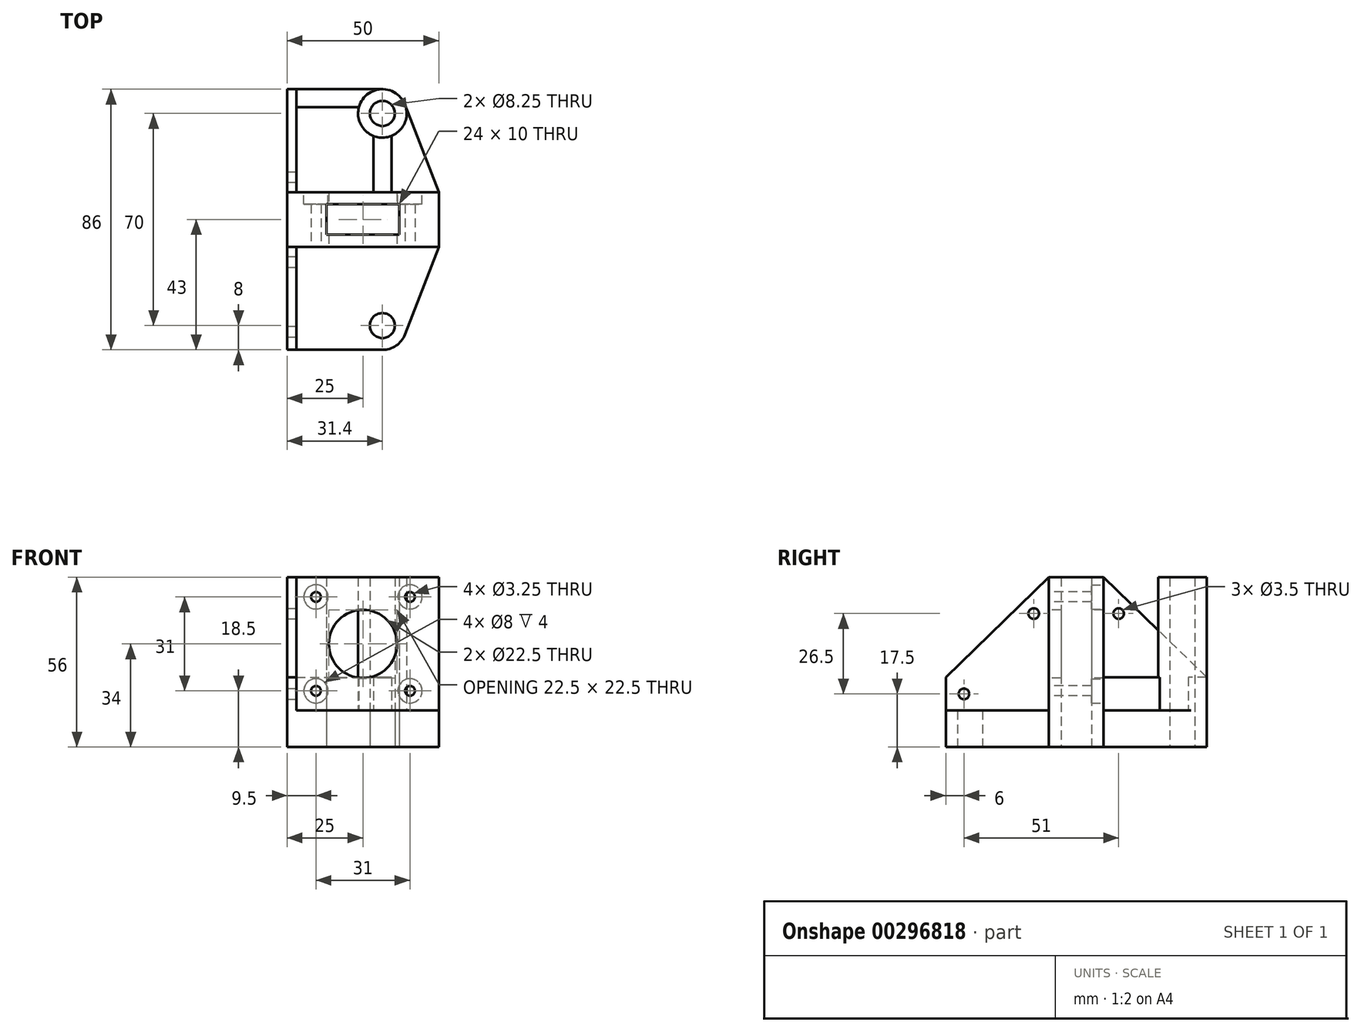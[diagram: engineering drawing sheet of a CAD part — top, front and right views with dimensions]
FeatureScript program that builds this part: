
annotation { "Feature Type Name" : "Feature", "Feature Type Description" : "" }
export const myFeature = defineFeature(function(context is Context, id is Id, definition is map)
    precondition{}
    {
        {
            var Q0;
            Q0=qCreatedBy(makeId("Top.planeOp"),FACE);
            var sketch = newSketch(context, id + "F0", { "sketchPlane" : qUnion([Q0])});
            skLineSegment(sketch, "E0.bottom", {"start": v(-25, 43) * mm, "end": v(6.4, 43) * mm});
            skLineSegment(sketch, "E0.top", {"start": v(-25, -43) * mm, "end": v(6.4, -43) * mm});
            skLineSegment(sketch, "E0.left", {"start": v(-25, 43) * mm, "end": v(-25, -43) * mm});
            skLineSegment(sketch, "E0.right", {"start": v(25, 9) * mm, "end": v(25, -9) * mm});
            skPoint(sketch, "E0.middle", {"position": v(0, 0) * mm});
            skArc(sketch, "E1", {"start": v(13.86, 37.88) * mm, "mid": v(10.93, 41.6) * mm, "end": v(6.4, 43) * mm});
            skLineSegment(sketch, "E2", {"start": v(0, 0) * mm, "end": v(-25, 0) * mm, "construction": true});
            skArc(sketch, "E3.MirrorC", {"start": v(13.86, -37.88) * mm, "mid": v(10.93, -41.6) * mm, "end": v(6.4, -43) * mm});
            skCircle(sketch, "E4", {"center": v(6.4, 35) * mm, "radius": 4.12 * mm});
            skCircle(sketch, "E5.MirrorC", {"center": v(6.4, -35) * mm, "radius": 4.12 * mm});
            skLineSegment(sketch, "E6.bottom", {"start": v(-12, 5) * mm, "end": v(12, 5) * mm});
            skLineSegment(sketch, "E6.top", {"start": v(-12, -5) * mm, "end": v(12, -5) * mm});
            skLineSegment(sketch, "E6.left", {"start": v(-12, 5) * mm, "end": v(-12, -5) * mm});
            skLineSegment(sketch, "E6.right", {"start": v(12, 5) * mm, "end": v(12, -5) * mm});
            skLineSegment(sketch, "E7", {"start": v(25, 9) * mm, "end": v(13.86, 37.88) * mm});
            skPoint(sketch, "E8.orphan", {"position": v(25, 43) * mm});
            skLineSegment(sketch, "E9.MirrorCS", {"start": v(25, -9) * mm, "end": v(13.86, -37.88) * mm});
            skPoint(sketch, "E10.orphan", {"position": v(25, -43) * mm});
            skSolve(sketch);
        }
        {
            var Q0;
            Q0=makeQuery(id+"F0.imprint","IMPRINT",FACE,{"disambiguationData":[TD([[makeQuery(id+"F0.imprint","IMPRINT",EDGE,{"derivedFrom":sQuery(id+"F0.wireOp",EDGE,"E0.bottom")}),-1.0]])]});
            extrude(context, id + "F1", {"entities" : qUnion([Q0]), "depth" : 12 * mm});
        }
        {
            var Q0;
            Q0=makeQuery(id+"F1.opExtrude","CAP_FACE",FACE,{"disambiguationData":[OSD([sQuery(id+"F0.wireOp",EDGE,"E0.bottom"),sQuery(id+"F0.wireOp",EDGE,"E0.top"),sQuery(id+"F0.wireOp",EDGE,"E0.left"),sQuery(id+"F0.wireOp",EDGE,"E0.right"),sQuery(id+"F0.wireOp",EDGE,"E1"),sQuery(id+"F0.wireOp",EDGE,"E3.MirrorC"),sQuery(id+"F0.wireOp",EDGE,"E4"),sQuery(id+"F0.wireOp",EDGE,"E5.MirrorC"),sQuery(id+"F0.wireOp",EDGE,"E6.bottom"),sQuery(id+"F0.wireOp",EDGE,"E6.top"),sQuery(id+"F0.wireOp",EDGE,"E6.left"),sQuery(id+"F0.wireOp",EDGE,"E6.right"),sQuery(id+"F0.wireOp",EDGE,"E7"),sQuery(id+"F0.wireOp",EDGE,"E9.MirrorCS")])],"isStart":false});
            var sketch = newSketch(context, id + "F2", { "sketchPlane" : qUnion([Q0])});
            skLineSegment(sketch, "E11.bottom", {"start": v(25, -9) * mm, "end": v(-25, -9) * mm});
            skLineSegment(sketch, "E11.top", {"start": v(25, 9) * mm, "end": v(-25, 9) * mm});
            skLineSegment(sketch, "E11.left", {"start": v(25, -9) * mm, "end": v(25, 9) * mm});
            skLineSegment(sketch, "E11.right", {"start": v(-25, -9) * mm, "end": v(-25, 9) * mm});
            skPoint(sketch, "E11.middle", {"position": v(0, 0) * mm});
            skLineSegment(sketch, "E12.0", {"start": v(-12, 5) * mm, "end": v(12, 5) * mm});
            skLineSegment(sketch, "E13.0", {"start": v(-12, 5) * mm, "end": v(-12, -5) * mm});
            skLineSegment(sketch, "E14.0", {"start": v(-12, -5) * mm, "end": v(12, -5) * mm});
            skLineSegment(sketch, "E15.0", {"start": v(12, 5) * mm, "end": v(12, -5) * mm});
            skSolve(sketch);
        }
        {
            var Q0;
            Q0=makeQuery(id+"F2.imprint","IMPRINT",FACE,{"disambiguationData":[TD([[makeQuery(id+"F2.imprint","IMPRINT",EDGE,{"derivedFrom":sQuery(id+"F2.wireOp",EDGE,"E11.bottom")}),-1.0]])]});
            extrude(context, id + "F3", {"entities" : qUnion([Q0]), "operationType" : NewBodyOperationType.ADD, "depth" : 44 * mm});
        }
        {
            var Q0;
            Q0=makeQuery(id+"F3.opExtrude","SWEPT_FACE",FACE,{"disambiguationData":[OSD([sQuery(id+"F2.wireOp",EDGE,"E11.bottom")])]});
            var sketch = newSketch(context, id + "F4", { "sketchPlane" : qUnion([Q0])});
            skLineSegment(sketch, "E16", {"start": v(-25, 34) * mm, "end": v(25, 34) * mm, "construction": true});
            skLineSegment(sketch, "E17", {"start": v(0, 56) * mm, "end": v(0, 12) * mm, "construction": true});
            skCircle(sketch, "E18", {"center": v(-15.5, 18.5) * mm, "radius": 1.63 * mm});
            skCircle(sketch, "E19.0.1.0", {"center": v(-15.5, 49.5) * mm, "radius": 1.63 * mm});
            skCircle(sketch, "E19.1.0.0", {"center": v(15.5, 18.5) * mm, "radius": 1.63 * mm});
            skCircle(sketch, "E19.1.1.0", {"center": v(15.5, 49.5) * mm, "radius": 1.63 * mm});
            skLineSegment(sketch, "E19.direction1", {"start": v(-15.5, 18.5) * mm, "end": v(15.5, 18.5) * mm, "construction": true});
            skLineSegment(sketch, "E19.direction2", {"start": v(-15.5, 18.5) * mm, "end": v(-15.5, 49.5) * mm, "construction": true});
            skCircle(sketch, "E20", {"center": v(0, 34) * mm, "radius": 11.25 * mm});
            skSolve(sketch);
        }
        {
            var Q0;
            Q0 = qSketchRegion(id + "F4", true);
            extrude(context, id + "F5", {"entities" : qUnion([Q0]), "operationType" : NewBodyOperationType.REMOVE, "endBound" : BoundingType.THROUGH_ALL, "oppositeDirection" : true, "depth" : 25 * mm});
        }
        {
            var Q0;
            Q0=makeQuery(id+"F3.boolean.opBoolean","MERGE",FACE,{"derivedFrom":[makeQuery(id+"F1.opExtrude","SWEPT_FACE",FACE,{"disambiguationData":[OSD([sQuery(id+"F0.wireOp",EDGE,"E0.left")])]}),makeQuery(id+"F3.opExtrude","SWEPT_FACE",FACE,{"disambiguationData":[OSD([sQuery(id+"F2.wireOp",EDGE,"E11.right")])]})]});
            var sketch = newSketch(context, id + "F6", { "sketchPlane" : qUnion([Q0])});
            skLineSegment(sketch, "E21.0", {"start": v(-43, 12) * mm, "end": v(-9, 12) * mm});
            skLineSegment(sketch, "E22.0", {"start": v(-9, 56) * mm, "end": v(-9, 12) * mm});
            skLineSegment(sketch, "E23.0", {"start": v(9, 56) * mm, "end": v(9, 12) * mm});
            skLineSegment(sketch, "E24.0", {"start": v(9, 12) * mm, "end": v(43, 12) * mm});
            skLineSegment(sketch, "E25", {"start": v(-43, 12) * mm, "end": v(-43, 23) * mm});
            skLineSegment(sketch, "E26", {"start": v(-43, 23) * mm, "end": v(-9, 56) * mm});
            skLineSegment(sketch, "E27", {"start": v(43, 12) * mm, "end": v(43, 23) * mm});
            skLineSegment(sketch, "E28", {"start": v(43, 23) * mm, "end": v(9, 56) * mm});
            skSolve(sketch);
        }
        {
            var Q0;
            Q0 = qSketchRegion(id + "F6", true);
            extrude(context, id + "F7", {"entities" : qUnion([Q0]), "operationType" : NewBodyOperationType.ADD, "oppositeDirection" : true, "depth" : 3 * mm});
        }
        {
            var Q0;
            {var subQ0=sQuery(id+"F0.wireOp",EDGE,"E1");var subQ1=sQuery(id+"F0.wireOp",EDGE,"E0.left");var subQ2=sQuery(id+"F0.wireOp",EDGE,"E0.right");var subQ3=sQuery(id+"F0.wireOp",EDGE,"E0.bottom");var subQ4=sQuery(id+"F0.wireOp",EDGE,"E4");var subQ5=sQuery(id+"F0.wireOp",EDGE,"E7");Q0=makeQuery(id+"F3.boolean.opBoolean","SPLIT",FACE,{"disambiguationData":[TD([makeQuery(id+"F1.opExtrude","SWEPT_FACE",FACE,{"disambiguationData":[OSD([subQ3])]})])],"derivedFrom":makeQuery(id+"F1.opExtrude","CAP_FACE",FACE,{"disambiguationData":[OSD([subQ3,sQuery(id+"F0.wireOp",EDGE,"E0.top"),subQ1,subQ2,subQ0,sQuery(id+"F0.wireOp",EDGE,"E3.MirrorC"),subQ4,sQuery(id+"F0.wireOp",EDGE,"E5.MirrorC"),sQuery(id+"F0.wireOp",EDGE,"E6.bottom"),sQuery(id+"F0.wireOp",EDGE,"E6.top"),sQuery(id+"F0.wireOp",EDGE,"E6.left"),sQuery(id+"F0.wireOp",EDGE,"E6.right"),subQ5,sQuery(id+"F0.wireOp",EDGE,"E9.MirrorCS")])],"isStart":false})});}
            var sketch = newSketch(context, id + "F8", { "sketchPlane" : qUnion([Q0])});
            skArc(sketch, "E29", {"start": v(9.4, 27.58) * mm, "mid": v(14.25, 36.53) * mm, "end": v(6.4, 43) * mm});
            skCircle(sketch, "E30.0", {"center": v(6.4, 35) * mm, "radius": 4.12 * mm});
            skLineSegment(sketch, "E31", {"start": v(6.4, 35) * mm, "end": v(6.4, 9) * mm, "construction": true});
            skLineSegment(sketch, "E32", {"start": v(6.4, 9) * mm, "end": v(3.4, 9) * mm});
            skLineSegment(sketch, "E33", {"start": v(3.4, 9) * mm, "end": v(3.4, 27.58) * mm});
            skLineSegment(sketch, "E34.MirrorCS", {"start": v(9.4, 9) * mm, "end": v(9.4, 27.58) * mm});
            skLineSegment(sketch, "E35.MirrorCS", {"start": v(6.4, 9) * mm, "end": v(9.4, 9) * mm});
            skLineSegment(sketch, "E36.0", {"start": v(-22, 43) * mm, "end": v(6.4, 43) * mm});
            skLineSegment(sketch, "E37", {"start": v(-22, 43) * mm, "end": v(-22, 37) * mm});
            skLineSegment(sketch, "E38", {"start": v(-22, 37) * mm, "end": v(-1.35, 37) * mm});
            skArc(sketch, "E39.trimOffspring", {"start": v(-1.35, 37) * mm, "mid": v(-0.74, 31.4) * mm, "end": v(3.4, 27.58) * mm});
            skSolve(sketch);
        }
        {
            var Q0;
            Q0=makeQuery(id+"F8.imprint","IMPRINT",FACE,{"disambiguationData":[TD([[makeQuery(id+"F8.imprint","IMPRINT",EDGE,{"derivedFrom":sQuery(id+"F8.wireOp",EDGE,"E30.0")}),-1.0]])]});
            var Q1;
            Q1=makeQuery(id+"F5.boolean.opBoolean","COPY",FACE,{"disambiguationData":[TD([makeQuery(id+"F1.opExtrude","SWEPT_FACE",FACE,{"disambiguationData":[OSD([sQuery(id+"F0.wireOp",EDGE,"E6.bottom")])]})])],"derivedFrom":makeQuery(id+"F5.opExtrude","SWEPT_FACE",FACE,{"disambiguationData":[OSD([sQuery(id+"F4.wireOp",EDGE,"E20")])]})});
            extrude(context, id + "F9", {"entities" : qUnion([Q0]), "operationType" : NewBodyOperationType.ADD, "endBoundEntityFace" : qUnion([Q1]), "depth" : 11 * mm});
        }
        {
            var Q0;
            Q0=makeQuery(id+"F3.opExtrude","SWEPT_FACE",FACE,{"disambiguationData":[OSD([sQuery(id+"F2.wireOp",EDGE,"E11.top")])]});
            var sketch = newSketch(context, id + "F10", { "sketchPlane" : qUnion([Q0])});
            skCircle(sketch, "E40", {"center": v(-15.5, 18.5) * mm, "radius": 4 * mm});
            skCircle(sketch, "E41.0.1.0", {"center": v(-15.5, 49.5) * mm, "radius": 4 * mm});
            skCircle(sketch, "E41.1.0.0", {"center": v(15.5, 18.5) * mm, "radius": 4 * mm});
            skCircle(sketch, "E41.1.1.0", {"center": v(15.5, 49.5) * mm, "radius": 4 * mm});
            skLineSegment(sketch, "E41.direction1", {"start": v(-15.5, 18.5) * mm, "end": v(15.5, 18.5) * mm, "construction": true});
            skLineSegment(sketch, "E41.direction2", {"start": v(-15.5, 18.5) * mm, "end": v(-15.5, 49.5) * mm, "construction": true});
            skSolve(sketch);
        }
        {
            var Q0;
            Q0 = qSketchRegion(id + "F10", true);
            extrude(context, id + "F11", {"entities" : qUnion([Q0]), "operationType" : NewBodyOperationType.REMOVE, "oppositeDirection" : true, "depth" : 4 * mm});
        }
        {
            var Q0;
            Q0=makeQuery(id+"F9.opExtrude","CAP_FACE",FACE,{"disambiguationData":[OSD([sQuery(id+"F8.wireOp",EDGE,"E29"),sQuery(id+"F8.wireOp",EDGE,"E30.0"),sQuery(id+"F8.wireOp",EDGE,"E32"),sQuery(id+"F8.wireOp",EDGE,"E33"),sQuery(id+"F8.wireOp",EDGE,"E34.MirrorCS"),sQuery(id+"F8.wireOp",EDGE,"E35.MirrorCS"),sQuery(id+"F8.wireOp",EDGE,"E36.0"),sQuery(id+"F8.wireOp",EDGE,"E37"),sQuery(id+"F8.wireOp",EDGE,"E38"),sQuery(id+"F8.wireOp",EDGE,"E39.trimOffspring")])],"isStart":false});
            var sketch = newSketch(context, id + "F12", { "sketchPlane" : qUnion([Q0])});
            skCircle(sketch, "E42", {"center": v(6.4, 35) * mm, "radius": 8 * mm});
            skCircle(sketch, "E43.0", {"center": v(6.4, 35) * mm, "radius": 4.12 * mm});
            skSolve(sketch);
        }
        {
            var Q0;
            Q0 = qSketchRegion(id + "F12", true);
            var Q1;
            Q1=makeQuery(id+"F3.opExtrude","CAP_FACE",FACE,{"disambiguationData":[OSD([sQuery(id+"F2.wireOp",EDGE,"E11.bottom"),sQuery(id+"F2.wireOp",EDGE,"E11.top"),sQuery(id+"F2.wireOp",EDGE,"E11.left"),sQuery(id+"F2.wireOp",EDGE,"E11.right"),sQuery(id+"F2.wireOp",EDGE,"E12.0"),sQuery(id+"F2.wireOp",EDGE,"E13.0"),sQuery(id+"F2.wireOp",EDGE,"E14.0"),sQuery(id+"F2.wireOp",EDGE,"E15.0")])],"isStart":false});
            extrude(context, id + "F13", {"entities" : qUnion([Q0]), "operationType" : NewBodyOperationType.ADD, "endBound" : BoundingType.UP_TO_SURFACE, "endBoundEntityFace" : qUnion([Q1]), "depth" : 12 * mm});
        }
        {
            var Q0;
            Q0=makeQuery(id+"F7.opExtrude","CAP_FACE",FACE,{"disambiguationData":[OSD([sQuery(id+"F6.wireOp",EDGE,"E23.0"),sQuery(id+"F6.wireOp",EDGE,"E24.0"),sQuery(id+"F6.wireOp",EDGE,"E27"),sQuery(id+"F6.wireOp",EDGE,"E28")])],"isStart":false});
            var sketch = newSketch(context, id + "F14", { "sketchPlane" : qUnion([Q0])});
            skCircle(sketch, "E44", {"center": v(-37, 17.5) * mm, "radius": 1.75 * mm});
            skPoint(sketch, "E44.centerSnap0", {"position": v(-43, 17.5) * mm});
            skCircle(sketch, "E45", {"center": v(-14, 44) * mm, "radius": 1.75 * mm});
            skLineSegment(sketch, "E46", {"start": v(0, 0) * mm, "end": v(0, 56.42) * mm, "construction": true});
            skCircle(sketch, "E47.MirrorC", {"center": v(14, 44) * mm, "radius": 1.75 * mm});
            skSolve(sketch);
        }
        {
            var Q0;
            Q0 = qSketchRegion(id + "F14", true);
            extrude(context, id + "F15", {"entities" : qUnion([Q0]), "operationType" : NewBodyOperationType.REMOVE, "oppositeDirection" : true, "depth" : 25 * mm});
        }
    });
